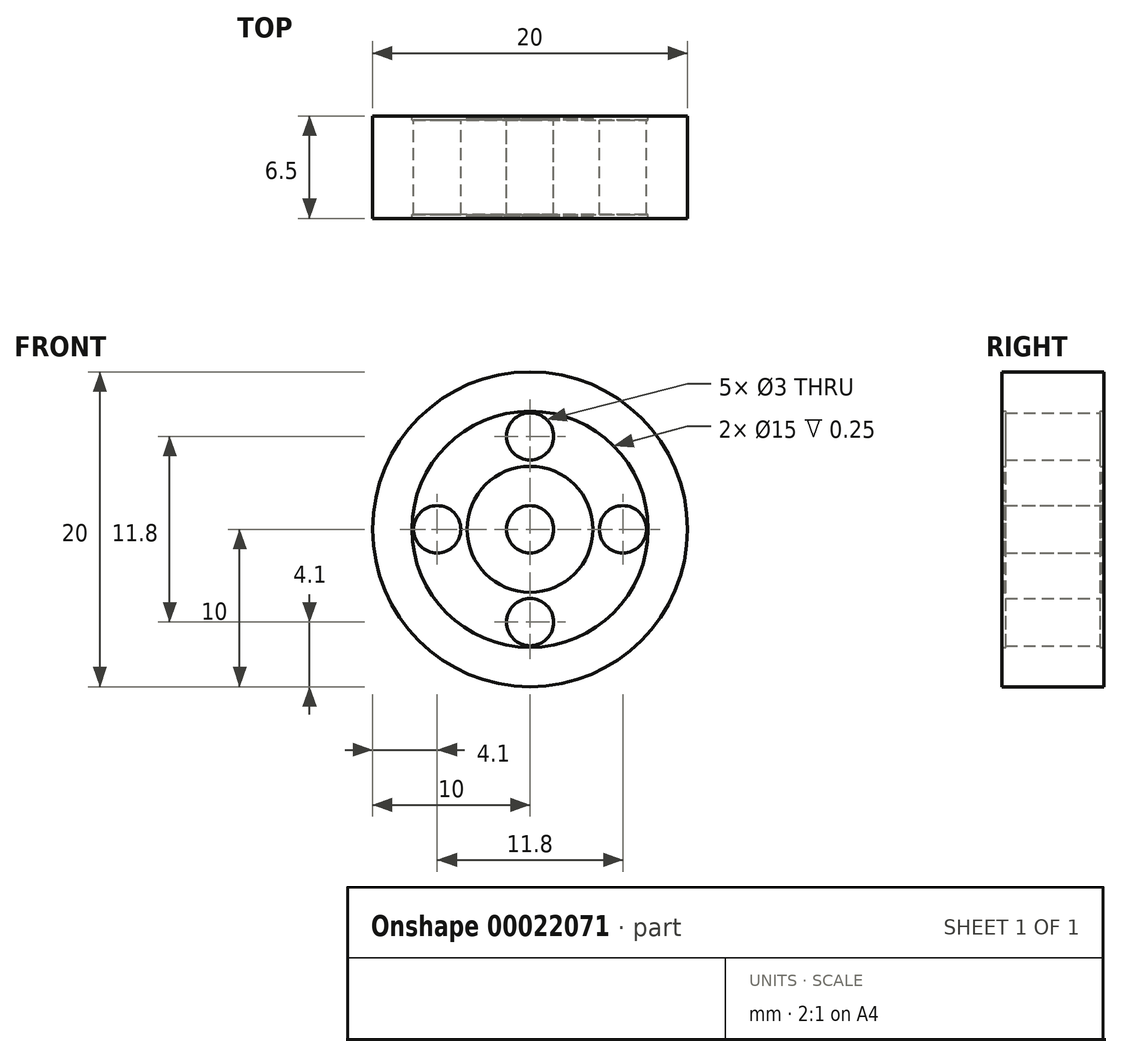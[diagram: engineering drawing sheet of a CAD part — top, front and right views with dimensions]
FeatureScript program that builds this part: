
annotation { "Feature Type Name" : "Feature", "Feature Type Description" : "" }
export const myFeature = defineFeature(function(context is Context, id is Id, definition is map)
    precondition{}
    {
        {
            var Q0;
            Q0=qCreatedBy(makeId("Front.planeOp"),FACE);
            var sketch = newSketch(context, id + "F0", { "sketchPlane" : qUnion([Q0])});
            skCircle(sketch, "E0", {"center": v(0, 0) * mm, "radius": 10 * mm});
            skCircle(sketch, "E1", {"center": v(0, 0) * mm, "radius": 4 * mm});
            skCircle(sketch, "E2", {"center": v(0, 0) * mm, "radius": 1.5 * mm});
            skCircle(sketch, "E3", {"center": v(0, 5.9) * mm, "radius": 1.5 * mm});
            skCircle(sketch, "E4.1.0", {"center": v(-5.9, 0) * mm, "radius": 1.5 * mm});
            skCircle(sketch, "E4.2.0", {"center": v(0, -5.9) * mm, "radius": 1.5 * mm});
            skCircle(sketch, "E4.3.0", {"center": v(5.9, 0) * mm, "radius": 1.5 * mm});
            skCircle(sketch, "E5", {"center": v(0, 0) * mm, "radius": 7.5 * mm});
            skSolve(sketch);
        }
        {
            var Q0;
            Q0 = qSketchRegion(id + "F0", true);
            extrude(context, id + "F1", {"entities" : qUnion([Q0]), "endBound" : BoundingType.SYMMETRIC, "depth" : 6.5 * mm});
        }
        {
            var Q0;
            Q0=makeQuery(id+"F0.imprint","IMPRINT",FACE,{"disambiguationData":[TD([[makeQuery(id+"F0.imprint","IMPRINT",EDGE,{"derivedFrom":sQuery(id+"F0.wireOp",EDGE,"E1")}),-1.0]])]});
            extrude(context, id + "F2", {"entities" : qUnion([Q0]), "operationType" : NewBodyOperationType.ADD, "endBound" : BoundingType.SYMMETRIC, "depth" : 6 * mm});
        }
        {
            var Q0;
            Q0=makeQuery(id+"F0.imprint","IMPRINT",FACE,{"disambiguationData":[TD([[makeQuery(id+"F0.imprint","IMPRINT",EDGE,{"derivedFrom":sQuery(id+"F0.wireOp",EDGE,"E1")}),1.0]])]});
            extrude(context, id + "F3", {"entities" : qUnion([Q0]), "operationType" : NewBodyOperationType.ADD, "endBound" : BoundingType.SYMMETRIC, "depth" : 6.25 * mm});
        }
    });
